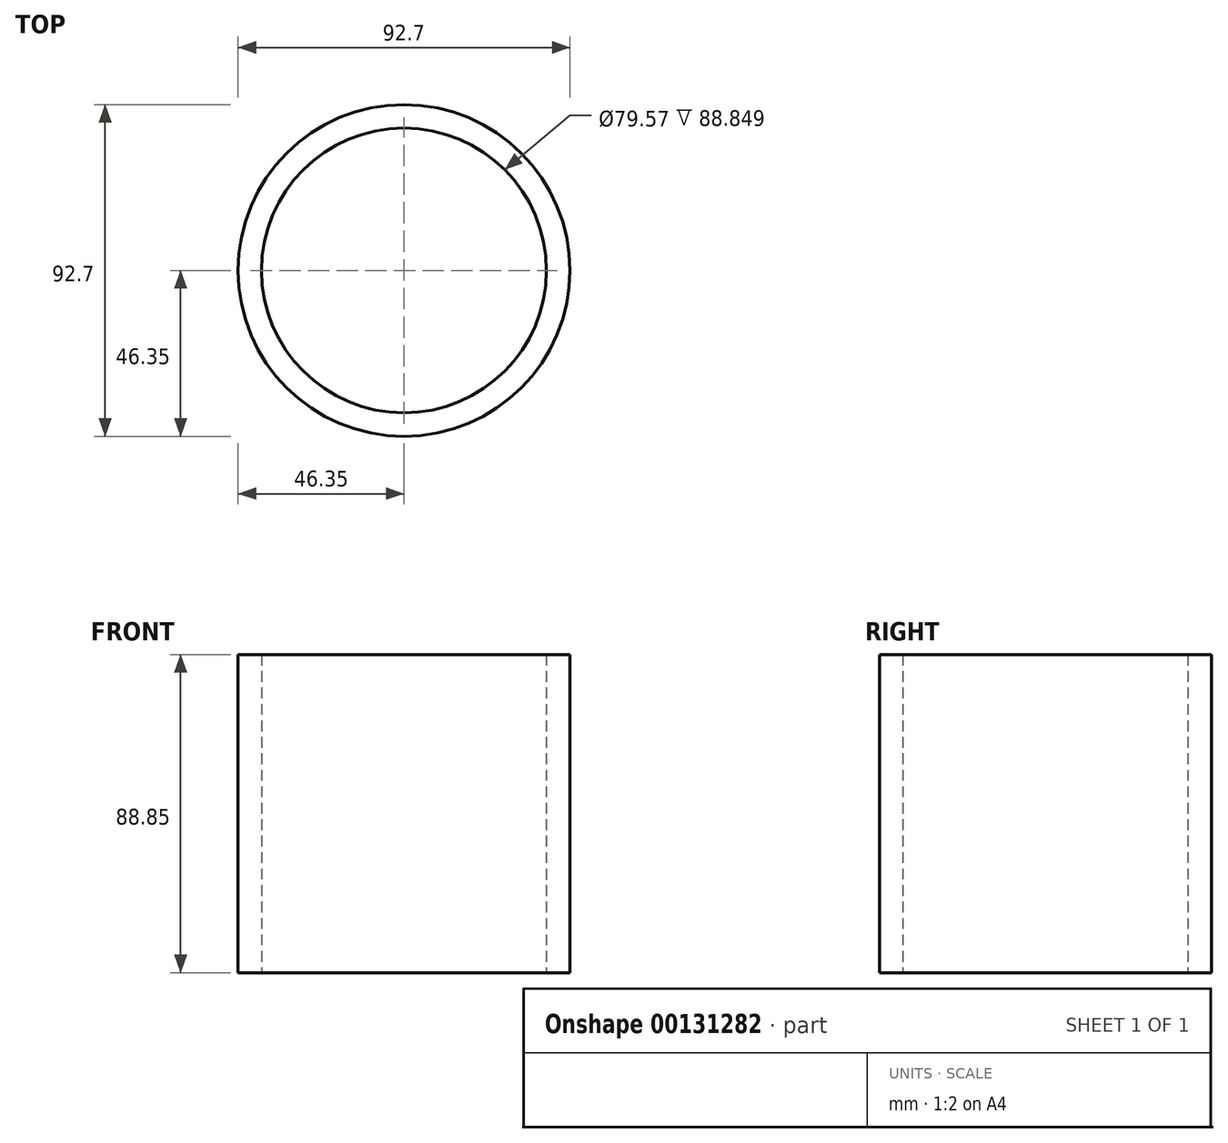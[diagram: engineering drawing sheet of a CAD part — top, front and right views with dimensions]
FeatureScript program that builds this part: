
annotation { "Feature Type Name" : "Feature", "Feature Type Description" : "" }
export const myFeature = defineFeature(function(context is Context, id is Id, definition is map)
    precondition{}
    {
        {
            var Q0;
            Q0=qCreatedBy(makeId("Top.planeOp"),FACE);
            var sketch = newSketch(context, id + "F0", { "sketchPlane" : qUnion([Q0])});
            skCircle(sketch, "E0", {"center": v(0, 0) * mm, "radius": 39.79 * mm});
            skCircle(sketch, "E1.0", {"center": v(0, 0) * mm, "radius": 46.35 * mm});
            skCircle(sketch, "E2", {"center": v(0, 0) * mm, "radius": 39.78 * mm});
            skSolve(sketch);
        }
        {
            var Q0;
            Q0=makeQuery(id+"F0.imprint","IMPRINT",FACE,{"disambiguationData":[TD([[makeQuery(id+"F0.imprint","IMPRINT",EDGE,{"derivedFrom":sQuery(id+"F0.wireOp",EDGE,"E0")}),-1.0]])]});
            extrude(context, id + "F1", {"entities" : qUnion([Q0]), "depth" : 88.85 * mm});
        }
    });
